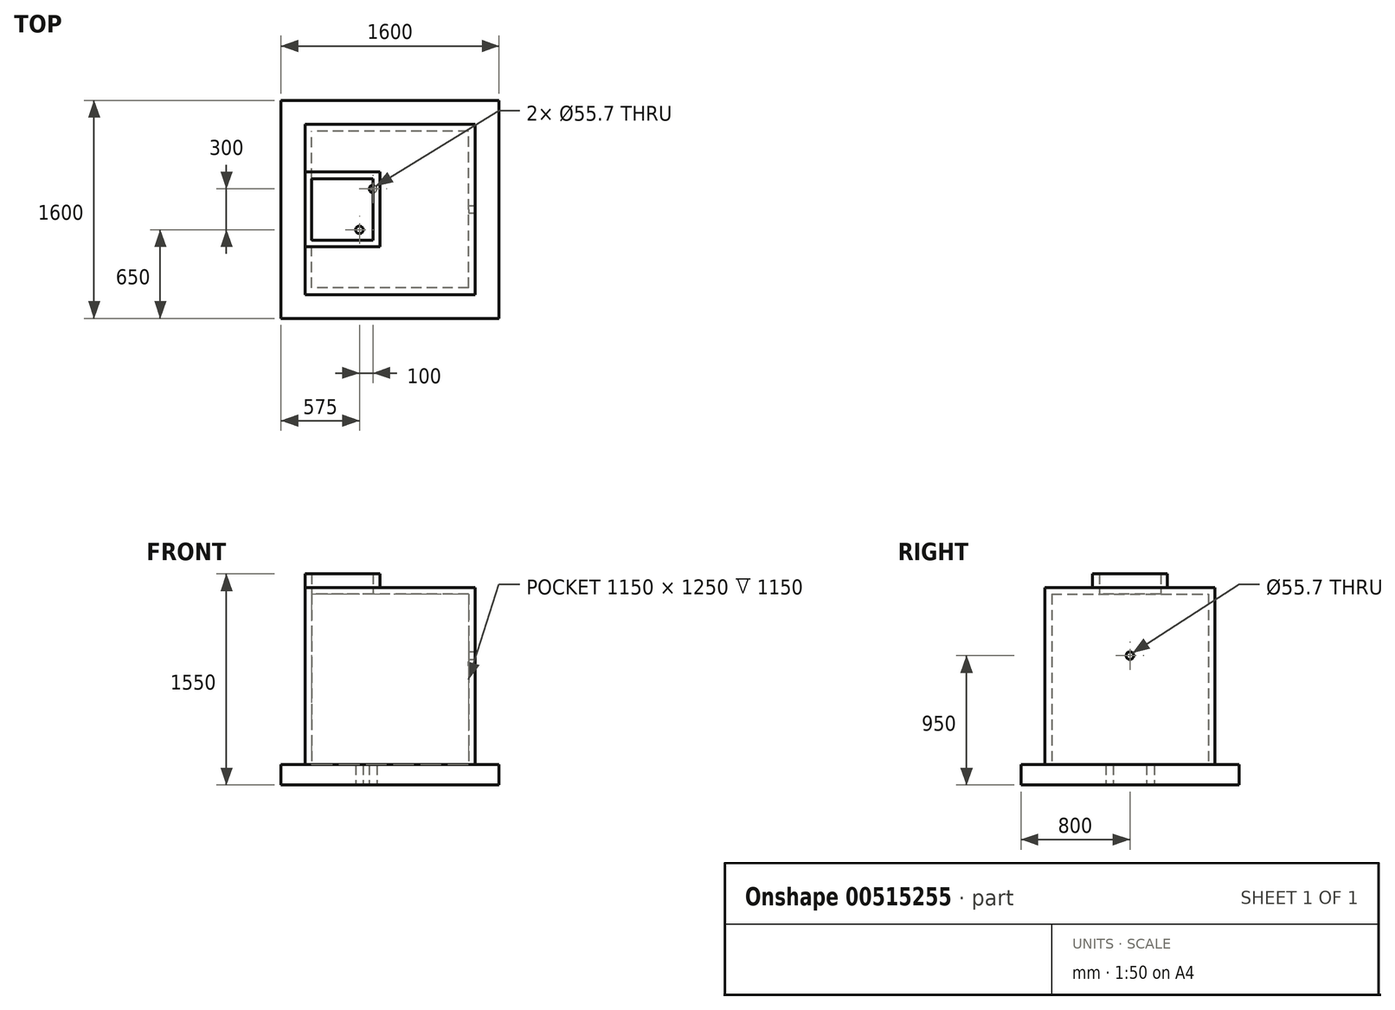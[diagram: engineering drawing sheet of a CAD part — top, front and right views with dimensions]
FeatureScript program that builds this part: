
annotation { "Feature Type Name" : "Feature", "Feature Type Description" : "" }
export const myFeature = defineFeature(function(context is Context, id is Id, definition is map)
    precondition{}
    {
        {
            var Q0;
            Q0=qCreatedBy(makeId("Top.planeOp"),FACE);
            var sketch = newSketch(context, id + "F0", { "sketchPlane" : qUnion([Q0])});
            skLineSegment(sketch, "E0.bottom", {"start": v(800, -800) * mm, "end": v(-800, -800) * mm});
            skLineSegment(sketch, "E0.top", {"start": v(800, 800) * mm, "end": v(-800, 800) * mm});
            skLineSegment(sketch, "E0.left", {"start": v(800, -800) * mm, "end": v(800, 800) * mm});
            skLineSegment(sketch, "E0.right", {"start": v(-800, -800) * mm, "end": v(-800, 800) * mm});
            skPoint(sketch, "E0.middle", {"position": v(0, 0) * mm});
            skSolve(sketch);
        }
        {
            var Q0;
            Q0=qCreatedBy(makeId("Top.planeOp"),FACE);
            var sketch = newSketch(context, id + "F1", { "sketchPlane" : qUnion([Q0])});
            skLineSegment(sketch, "E1.bottom", {"start": v(625, -625) * mm, "end": v(-625, -625) * mm});
            skLineSegment(sketch, "E1.top", {"start": v(625, 625) * mm, "end": v(-625, 625) * mm});
            skLineSegment(sketch, "E1.left", {"start": v(625, -625) * mm, "end": v(625, 625) * mm});
            skLineSegment(sketch, "E1.right", {"start": v(-625, -625) * mm, "end": v(-625, 625) * mm});
            skPoint(sketch, "E1.middle", {"position": v(0, 0) * mm});
            skLineSegment(sketch, "E2.bottom", {"start": v(575, -575) * mm, "end": v(-575, -575) * mm});
            skLineSegment(sketch, "E2.top", {"start": v(575, 575) * mm, "end": v(-575, 575) * mm});
            skLineSegment(sketch, "E2.left", {"start": v(-575, -575) * mm, "end": v(-575, 575) * mm});
            skLineSegment(sketch, "E2.right", {"start": v(575, -575) * mm, "end": v(575, 575) * mm});
            skSolve(sketch);
        }
        {
            var Q0;
            Q0=makeQuery(id+"F0.imprint","IMPRINT",FACE,{"disambiguationData":[TD([[makeQuery(id+"F0.imprint","IMPRINT",EDGE,{"derivedFrom":sQuery(id+"F0.wireOp",EDGE,"E0.bottom")}),-1.0]])]});
            extrude(context, id + "F2", {"entities" : qUnion([Q0]), "oppositeDirection" : true, "depth" : 150 * mm, "offsetDistance" : 25 * mm});
        }
        {
            var Q0;
            Q0=makeQuery(id+"F1.imprint","IMPRINT",FACE,{"disambiguationData":[TD([[makeQuery(id+"F1.imprint","IMPRINT",EDGE,{"derivedFrom":sQuery(id+"F1.wireOp",EDGE,"E1.bottom")}),-1.0]])]});
            extrude(context, id + "F3", {"entities" : qUnion([Q0]), "operationType" : NewBodyOperationType.ADD, "depth" : 1250 * mm, "offsetDistance" : 25 * mm});
        }
        {
            var Q0;
            Q0=makeQuery(id+"F3.opExtrude","CAP_FACE",FACE,{"disambiguationData":[OSD([sQuery(id+"F1.wireOp",EDGE,"E1.bottom"),sQuery(id+"F1.wireOp",EDGE,"E1.top"),sQuery(id+"F1.wireOp",EDGE,"E1.left"),sQuery(id+"F1.wireOp",EDGE,"E1.right"),sQuery(id+"F1.wireOp",EDGE,"E2.bottom"),sQuery(id+"F1.wireOp",EDGE,"E2.top"),sQuery(id+"F1.wireOp",EDGE,"E2.left"),sQuery(id+"F1.wireOp",EDGE,"E2.right")])],"isStart":false});
            var sketch = newSketch(context, id + "F4", { "sketchPlane" : qUnion([Q0])});
            skLineSegment(sketch, "E3.0", {"start": v(625, -625) * mm, "end": v(625, 625) * mm});
            skLineSegment(sketch, "E4.0", {"start": v(625, 625) * mm, "end": v(-625, 625) * mm});
            skLineSegment(sketch, "E5.0", {"start": v(625, -625) * mm, "end": v(-625, -625) * mm});
            skLineSegment(sketch, "E6.0.0", {"start": v(-625, 625) * mm, "end": v(-625, -625) * mm});
            skLineSegment(sketch, "E6.0.2", {"start": v(-625, -625) * mm, "end": v(-625, 625) * mm});
            skLineSegment(sketch, "E7.bottom", {"start": v(-125, 225) * mm, "end": v(-575, 225) * mm});
            skLineSegment(sketch, "E7.top", {"start": v(-125, -225) * mm, "end": v(-575, -225) * mm});
            skLineSegment(sketch, "E7.left", {"start": v(-125, 225) * mm, "end": v(-125, -225) * mm});
            skLineSegment(sketch, "E7.right", {"start": v(-575, 225) * mm, "end": v(-575, -225) * mm});
            skSolve(sketch);
        }
        {
            var Q0;
            Q0 = qSketchRegion(id + "F4", true);
            extrude(context, id + "F5", {"entities" : qUnion([Q0]), "operationType" : NewBodyOperationType.ADD, "depth" : 50 * mm, "offsetDistance" : 25 * mm});
        }
        {
            var Q0;
            Q0=makeQuery(id+"F5.opExtrude","CAP_FACE",FACE,{"disambiguationData":[OSD([sQuery(id+"F4.wireOp",EDGE,"E3.0"),sQuery(id+"F4.wireOp",EDGE,"E4.0"),sQuery(id+"F4.wireOp",EDGE,"E5.0"),sQuery(id+"F4.wireOp",EDGE,"E6.0.2"),sQuery(id+"F4.wireOp",EDGE,"E7.bottom"),sQuery(id+"F4.wireOp",EDGE,"E7.top"),sQuery(id+"F4.wireOp",EDGE,"E7.left"),sQuery(id+"F4.wireOp",EDGE,"E7.right")])],"isStart":false});
            var sketch = newSketch(context, id + "F6", { "sketchPlane" : qUnion([Q0])});
            skLineSegment(sketch, "E8.bottom", {"start": v(-625, 275) * mm, "end": v(-75, 275) * mm});
            skLineSegment(sketch, "E8.top", {"start": v(-625, -275) * mm, "end": v(-75, -275) * mm});
            skLineSegment(sketch, "E8.left", {"start": v(-625, 275) * mm, "end": v(-625, -275) * mm});
            skLineSegment(sketch, "E8.right", {"start": v(-75, 275) * mm, "end": v(-75, -275) * mm});
            skLineSegment(sketch, "E9.0", {"start": v(-125, 225) * mm, "end": v(-125, -225) * mm});
            skLineSegment(sketch, "E10.0", {"start": v(-125, -225) * mm, "end": v(-575, -225) * mm});
            skLineSegment(sketch, "E11.0", {"start": v(-575, -225) * mm, "end": v(-575, 225) * mm});
            skLineSegment(sketch, "E12.0", {"start": v(-125, 225) * mm, "end": v(-575, 225) * mm});
            skSolve(sketch);
        }
        {
            var Q0;
            Q0=makeQuery(id+"F6.imprint","IMPRINT",FACE,{"disambiguationData":[TD([[makeQuery(id+"F6.imprint","IMPRINT",EDGE,{"derivedFrom":sQuery(id+"F6.wireOp",EDGE,"E8.bottom")}),-1.0]])]});
            extrude(context, id + "F7", {"entities" : qUnion([Q0]), "operationType" : NewBodyOperationType.ADD, "depth" : 100 * mm, "offsetDistance" : 25 * mm});
        }
        {
            var Q0;
            Q0=makeQuery(id+"F5.boolean.opBoolean","MERGE",FACE,{"derivedFrom":[makeQuery(id+"F3.opExtrude","SWEPT_FACE",FACE,{"disambiguationData":[OSD([sQuery(id+"F1.wireOp",EDGE,"E1.left")])]}),makeQuery(id+"F5.opExtrude","SWEPT_FACE",FACE,{"disambiguationData":[OSD([sQuery(id+"F4.wireOp",EDGE,"E3.0")])]})]});
            var sketch = newSketch(context, id + "F8", { "sketchPlane" : qUnion([Q0])});
            skCircle(sketch, "E13", {"center": v(0, 800) * mm, "radius": 27.85 * mm});
            skSolve(sketch);
        }
        {
            var Q0;
            Q0=makeQuery(id+"F8.imprint","IMPRINT",FACE,{"disambiguationData":[TD([[makeQuery(id+"F8.imprint","IMPRINT",EDGE,{"derivedFrom":sQuery(id+"F8.wireOp",EDGE,"E13")}),1.0]])]});
            extrude(context, id + "F9", {"entities" : qUnion([Q0]), "operationType" : NewBodyOperationType.REMOVE, "oppositeDirection" : true, "depth" : 100 * mm, "offsetDistance" : 25 * mm});
        }
        {
            var Q0;
            Q0=makeQuery(id+"F2.opExtrude","CAP_FACE",FACE,{"disambiguationData":[OSD([sQuery(id+"F0.wireOp",EDGE,"E0.bottom"),sQuery(id+"F0.wireOp",EDGE,"E0.top"),sQuery(id+"F0.wireOp",EDGE,"E0.left"),sQuery(id+"F0.wireOp",EDGE,"E0.right")])],"isStart":false});
            var sketch = newSketch(context, id + "F10", { "sketchPlane" : qUnion([Q0])});
            skCircle(sketch, "E14", {"center": v(-125, -150) * mm, "radius": 27.85 * mm});
            skCircle(sketch, "E15", {"center": v(-225, 150) * mm, "radius": 27.85 * mm});
            skSolve(sketch);
        }
        {
            var Q0;
            Q0 = qSketchRegion(id + "F10", true);
            extrude(context, id + "F11", {"entities" : qUnion([Q0]), "operationType" : NewBodyOperationType.REMOVE, "oppositeDirection" : true, "depth" : 200 * mm, "offsetDistance" : 25 * mm});
        }
    });
